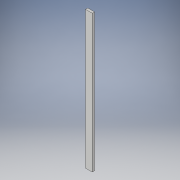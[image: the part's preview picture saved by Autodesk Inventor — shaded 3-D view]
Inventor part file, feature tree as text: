
AUTODESK INVENTOR PART (.ipt)
format: ipt  version: 2018 (Build 220112000, 112)  size: 92,672 bytes
history: native  units: in
note: dims shown in document units (in); Inventor stores cm internally (conversion verified against a paired STEP export)
features: extrude x1, sketch x1
ambient origin geometry x8: Origin, YZ Plane, XZ Plane, XY Plane, X Axis, Y Axis, Z Axis, Center Point
bodies: Solid1 (feature_tree)
feature tree (2):
  extrude  "Extrusion1"  Depth=11.811in
  sketch  "Sketch1"  dims[d0=0.5906in d1=11.811in d2=0.1969in d3=0.0in]
